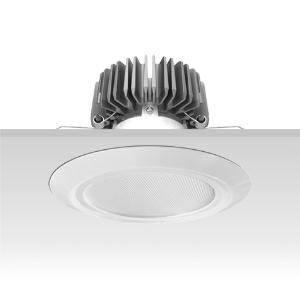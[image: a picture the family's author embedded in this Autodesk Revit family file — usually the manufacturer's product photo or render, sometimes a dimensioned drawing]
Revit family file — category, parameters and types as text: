
# Revit family: 3f_filippi_-_3f_reno_bianco_ampio_3f_filippi_-_30683_a01037_-_3f_reno_200_wh_3000-930_dali_wide___vs_wh_885b
name_source: partatom
category: Lighting Fixtures
units: mm (PartAtom-declared; Revit-internal decimal feet)

## family parameters
Cut with Voids When Loaded = No
Host = Face
Light Source = No
Part Type = Normal
Room Calculation Point = No
Round Connector Dimension = Use Diameter
Shared = No

## types (1)
- 3F Filippi - 3F Reno Bianco Ampio (1 x LED, 2320 lm, 37 W, 3000 K)
    Apparent Load = 37 VA
    Approval mark = CE
    CIE Flux Codes = 75 94 99 100 100
    Color Rendering = 90
    Color Temperature = 3000 K
    Control Gear = Electronic transformer
    Default Elevation = 1800 mm
    Description = ILLUMINOTECHNICAL
Luminous efficiency 100% (DLOR 100%, ULOR 0%).
Initial luminous flux of the luminaire 2320 lm.
Direct symmetric wide distribution.
Installation Interdistance Transv.D = 1.16 x hu - Long.D = 1.14 x hu.
Tabular UGR (CIE 117 - 4H-8H; S=0.25H; 70/50/20): RUG 21.5 - 21.4.
Beam angle: 74° - 74°.
Luminous efficacy 63 lm/W.
Lifetime (L90/B10): 30000 h. (tq+25°C)
Lifetime (L85/B10): 50000 h. (tq+25°C)
Lifetime (L70/B10): 80000 h. (tq+25°C)
Sudden decreased luminous flux after 50000 hours: 0% (C0).
Photobiological safety in compliance with IEC/TR 62778: RG0 risk exempt, (IEC 62471).
In compliance with IEC/EN 62722-2-1 - IEC/EN 62717 standards.

SOURCE
Compact LED module 3000/930.
Energy efficiency class (UE 2019/2020 - UE 2019/2015): E.
CIE 13.3 Colour rendering index: CRI >90 (R9 >50%).
IES TM-30 Fidelity Index: Rf = 92 Rg = 101.
CCT nominal colour temperature 3000 K.
Colour initial tolerance (MacAdam): SDCM 3.
Zhaga Book 3 compliant.

MECHANICAL
Passive heat dissipator in die-casting aluminium, oversized, for optimum thermal management of the LED module.
Parabolic element with graduated/concentric rings in white polycarbonate.
Transparent external lens with glossy and satin differentiated surfaces, with a cooling and anti-insect system in methacrylate (PMMA).
Fastening spring clips in stainless steel.
Dimensions: diameter 226 mm, height 146 mm. Weight 1.85 kg.
IP44 protection degree for exposed part, IP20 for recessed part.
Mechanical strength to impacts IK06 (1 joule).
Glow-wire test resistance 650°C.

ELECTRICAL
Wiring on a separate unit.
Halogen Free DALI-2 DATI (Parts 251, 252, 253), PUSH-DIM, electronic wiring 230V-50/60Hz, power factor 0.97 at full load, THD <25%, constant output current, SELV, class II, 1 driver, 1 DALI addresse.
Power of the luminaire 37 W.
ENEC - CE.
SAFE FLICKER: PstLM=<1 and SVM=<0.4 (IEC TR 61547-1 and IEC TR 63158), to ensure a more comfortable and safe light.
Luminaire compliant with EN 60598-2-22 for power supply from a centralised emergency system CPSS (Central Power Supply System), not incorporated in the luminaire - high risk areas excluded. The default power and flux are 100% in AC and 100% in DC.
Ambient temperature from 0°C to +25°C.
Temperature class T6 max 85°C.
Relative humidity UR: <85%.

INSTALLATION
Pull-up recessed fitting.
False ceiling carving: 200 mm.
All accessories dedicated to this product are available on the Catalog and on our website www.3F-Filippi.com.

ACCESSORIES
A01037 - Anti-glare microprismatic VS moulded glass, tempered, not flammable, locked and in line with the trim, in white polycarbonate.

APPLICATIONS
Environments: architectural, commercial, exhibition areas, transit areas, corridors, shops, display windows, service areas.
In false ceilings with narrow voids.

LIGHT MANAGEMENT
Recommended minimum setting: 10%.
The luminaire, equipped with (DALI-2 DATI) driver, can be controlled manually with 3F Easy Dim technology or automatically/manually with wired or wireless DALI/D2D control systems.
The D2D driver guarantees interoperability with other devices with the same certification by making the following information available:
Device Data (Part 251), Energy Report (Part 252), Diagnosis & Maintenance (Part 253).
In electrical systems without a regulation system (manual or automatic) and DALI bus, a suitable jumper must be made on the DA-DA terminals of the appliance.

WARNING
Luminaire designed for disposal/recycling at end-of-life.
Replaceable (LED only) light source by a professional. Replaceable control gear by a professional.
    Height = 0 mm  [stored 0 ft]
    Lamp = 1 x LED
    Lamp Light Flux = 2320 lm
    Lamp Power = 37 W
    Lamp count = 1
    Length = 226 mm
    Lifetime = 50000 h
    Luminous efficacy = 63 lm/W
    Manufacturer = 3F Filippi
    ModVariant = No
    Model = 3F Filippi - 30683+A01037 - 3F Reno 200 WH 3000-930 DALI WIDE + VS WH
    Mounting Place = Ceiling
    Mounting Type = Recessed
    Number of Poles = 1
    OnlyDefault = Yes
    Power Factor = 1
    Product Name = 3F Filippi - 3F Reno Bianco Ampio
    Product group = recessed luminaire
    ProductGroupID = 4
    Protection Class = Protection class II
    Protection Degree = IP 20
    RLX_Detail_Level = 1
    RLX_Emergency_Light_Flux = 0 lm
    RLX_Emergency_Type = 0
    RLX_Emergency_Type_DB = No
    RlxData = <blob elided: 96409 chars, md5=50d97de3>
    Socket = socket
    Standby Power = 0 W
    System Light Flux = 2320 lm
    System Power = 37 W
    Type Comments = Product without accessories
    Type Image = 3ffilippi_3f_reno_200_wh_vs_smp.jpg
    URL = http://relux.com
    VarID = ---
    Voltage = 0 V
    Weight = 0.00 kg
    Width = 0 mm  [stored 0 ft]

note: [stored X ft] marks values corroborated as IEEE doubles in the binary element streams (Revit-internal decimal feet)

## geometry (parser evidence)
native form markers: Blend x4, Sweep x12
no freeform markers — native parametric forms only
